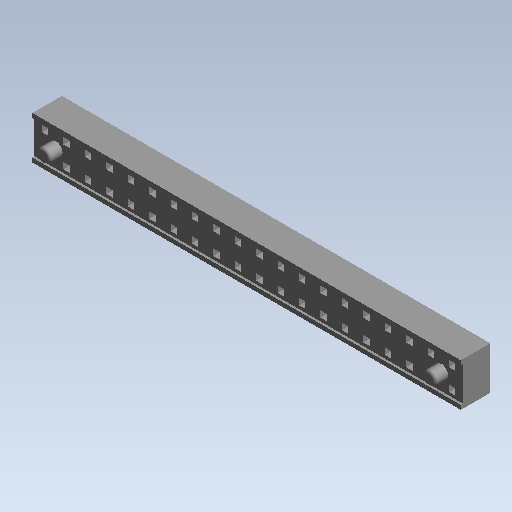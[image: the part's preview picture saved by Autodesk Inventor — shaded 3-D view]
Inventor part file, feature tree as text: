
AUTODESK INVENTOR PART (.ipt)
format: ipt  version: 2021 (Build 250183000, 183)  size: 378,368 bytes
history: native  units: mm (DEFAULTED — no unit token found)
features: other x14, sketch x5, extrude x3, revolve x2, pattern_linear x1
ambient origin geometry x8: Origin, YZ Plane, XZ Plane, XY Plane, X Axis, Y Axis, Z Axis, Center Point
bodies: Solid1 (feature_tree)
feature tree (25):
  extrude  "Extrusion1"  Depth=50.8mm TaperAngle=0.0deg
  extrude  "Extrusion2"  TaperAngle=360.0deg  [1 undecoded]
  revolve  "Revolution1"  [1 undecoded]
  revolve  "Revolution2"  [1 undecoded]
  extrude  "Extrusion3"  [1 undecoded]
  pattern_linear  "Rectangular Pattern1"  [2 undecoded]
  other  "socket_to_dummy_XY"
  other  "socket_to_dummy_YZ"
  other  "socket_to_dummy_ZX"
  other  "socket_to_dummy_X"
  other  "socket_to_dummy_Y"
  other  "socket_to_dummy_Z"
  other  "socket_to_dummy_Center"
  other  "socket_to_pad_XY"
  other  "socket_to_pad_YZ"
  other  "socket_to_pad_ZX"
  other  "socket_to_pad_X"
  other  "socket_to_pad_Y"
  other  "socket_to_pad_Z"
  other  "socket_to_pad_Center"
  sketch  "Sketch_1"  dims[d0=3.5052mm d1=0.0mm d2=50.8mm d3=0.0mm]
  sketch  "Sketch_4"  dims[d4=360.0deg d5=360.0deg]
  sketch  "Sketch_9"  dims[d6=1.27mm d7=0.0mm d8=190.0mm d10=2.54mm d11=10.0mm d13=0.0mm]
  sketch  "Sketch_10"  dims[d14=0.0mm]
  sketch  "Sketch_11"
note: 6 required parameter values undecoded (feature->parameter linkage not recoverable at this tier; creation-order binding heuristic only, values carry confidence <= 0.55)